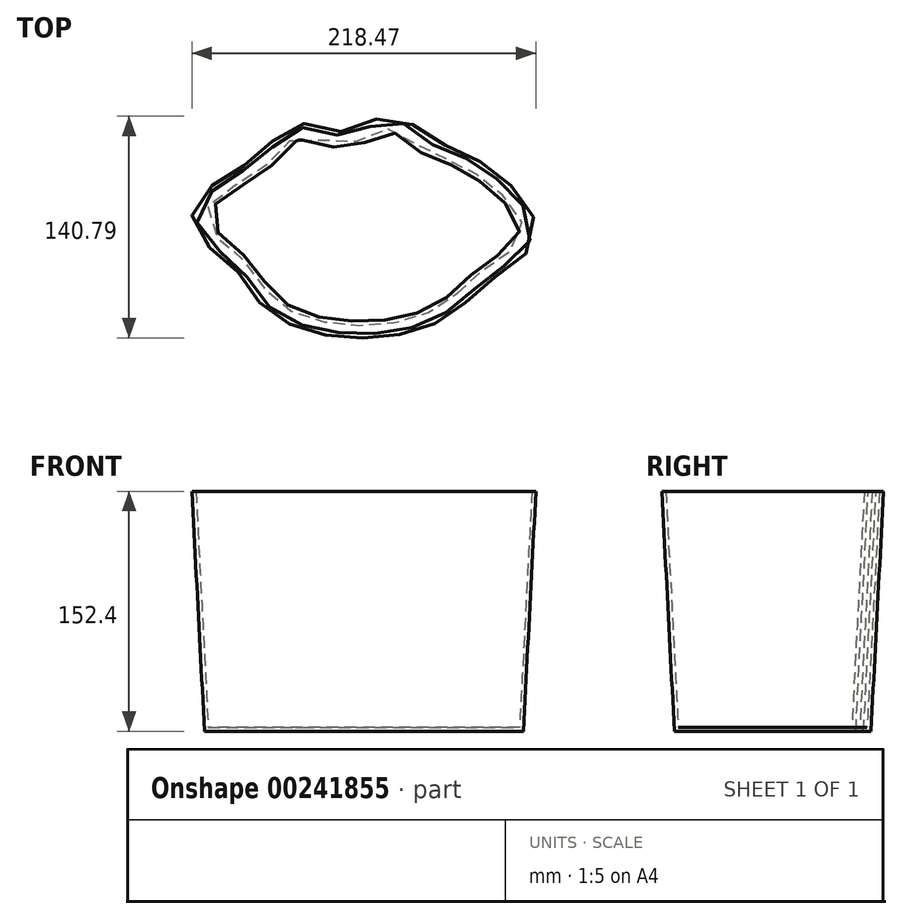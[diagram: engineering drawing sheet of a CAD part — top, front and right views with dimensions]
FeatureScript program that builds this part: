
annotation { "Feature Type Name" : "Feature", "Feature Type Description" : "" }
export const myFeature = defineFeature(function(context is Context, id is Id, definition is map)
    precondition{}
    {
        {
            var Q0;
            Q0=qCreatedBy(makeId("Top.planeOp"),FACE);
            var sketch = newSketch(context, id + "F0", { "sketchPlane" : qUnion([Q0])});
            skPoint(sketch, "E0.visualSharp", {"position": v(-76.45, 50.74) * mm});
            skPoint(sketch, "E1.visualSharp", {"position": v(75.85, 45.18) * mm});
            skPoint(sketch, "E2.visualSharp", {"position": v(75.85, -56.42) * mm});
            skPoint(sketch, "E3.visualSharp", {"position": v(-64.82, -50.19) * mm});
            skFitSpline(sketch, "E4", {"points": [v(-45.74, 49.9) * mm, v(-15.55, 45.1) * mm, v(13.91, 54.69) * mm, v(32.12, 42.47) * mm, v(58.47, 30.97) * mm, v(97.03, -9.75) * mm, v(72.84, -33.94) * mm, v(55.11, -49.75) * mm, v(25.17, -66.28) * mm, v(-34.72, -66.76) * mm, v(-64.82, -50.19) * mm, v(-78.55, -30.83) * mm, v(-105.42, 0) * mm, v(-65.42, 32.17) * mm, v(-45.74, 49.9) * mm]});
            skPoint(sketch, "E1.filletArc.center.orphan", {"position": v(58.47, 32.17) * mm});
            skSolve(sketch);
        }
        {
            var Q0;
            Q0=makeQuery(id+"F0.imprint","IMPRINT",FACE,{"disambiguationData":[TD([[makeQuery(id+"F0.imprint","IMPRINT",EDGE,{"derivedFrom":sQuery(id+"F0.wireOp",EDGE,"E4")}),-1.0]])]});
            extrude(context, id + "F1", {"entities" : qUnion([Q0]), "depth" : 152.4 * mm, "hasDraft" : true, "draftAngle" : 3 * degree});
        }
        {
            var Q0;
            Q0=makeQuery(id+"F1.opExtrude","CAP_FACE",FACE,{"disambiguationData":[OSD([sQuery(id+"F0.wireOp",EDGE,"E4")])],"isStart":false});
            shell(context, id + "F2", {"entities" : qUnion([Q0]), "thickness" : 2.54 * mm});
        }
    });
